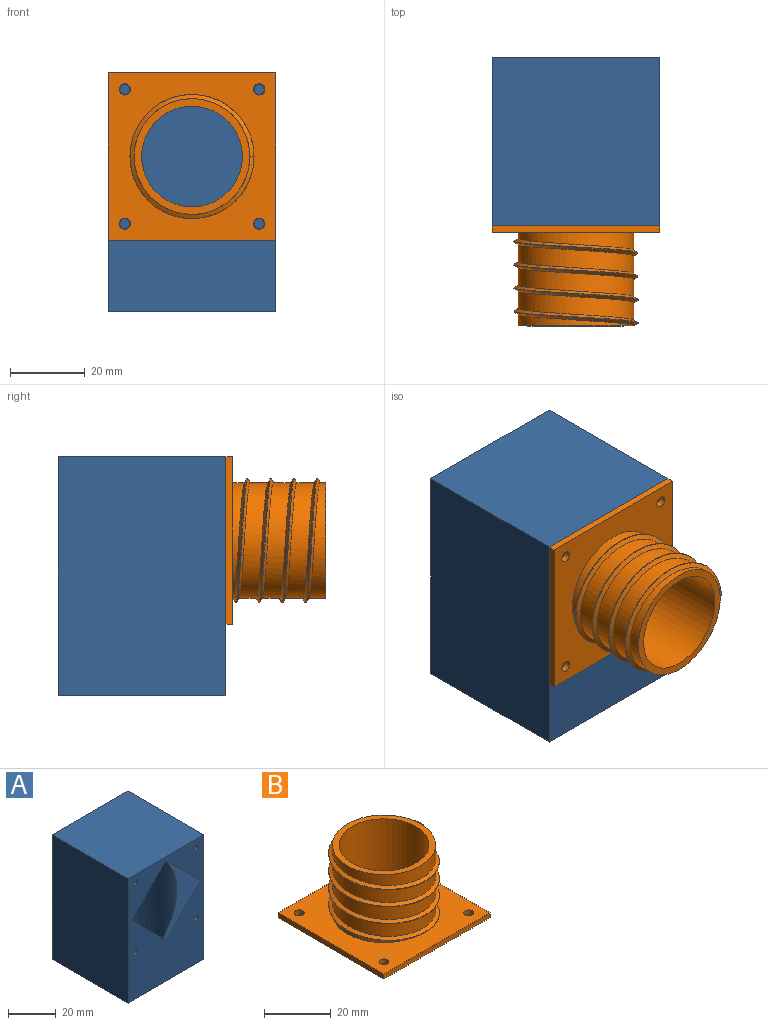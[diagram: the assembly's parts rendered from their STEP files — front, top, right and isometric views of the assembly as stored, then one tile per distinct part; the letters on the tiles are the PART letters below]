
ASSEMBLY  parts=2 mates=1
PART A: 22 faces, bbox 45x45x64 mm
  f0: plane 22.5x20.5mm, normal (0.71,0,0.71), area 185.5mm2, adj f5,f9,f11,f21
  f1: plane 20.5x20.5mm, normal (-0.71,0,0.71), area 127.5mm2, adj f8,f12,f21
  f2: plane 64x45mm, normal (1,0,0), area 2880mm2, adj f3,f5,f6,f7
  f3: plane 64x45mm, normal (0,1,0), area 2880mm2, adj f2,f4,f6,f7
  f4: plane 64x45mm, normal (-1,0,0), area 2880mm2, adj f3,f5,f6,f7
  f5: plane 64x45mm, normal (0,-1,0), area 2016.6mm2, adj f0,f2,f4,f6,f7,f8,f9,f11
  f6: plane 45x45mm, normal (0,0,1), area 2025mm2, adj f2,f3,f4,f5
  f7: plane 45x45mm, normal (0,0,-1), area 704.7mm2, adj f2,f3,f4,f5,f21
  f8: plane 43x20.5mm, normal (-0.71,0,-0.71), area 1246.6mm2, adj f1,f5,f9,f11,f12
  f9: plane 43x20.5mm, normal (0.71,0,-0.71), area 1246.6mm2, adj f0,f5,f8,f10,f12
  f10: plane 20.5x20.5mm, normal (0.71,0,0.71), area 127.5mm2, adj f9,f12,f21
  f11: plane 22.5x20.5mm, normal (-0.71,0,0.71), area 185.5mm2, adj f0,f5,f8,f21
  f12: plane 41x41mm, normal (0,-1,0), area 840.5mm2, adj f1,f8,f9,f10
  f13: cylinder r=1.35mm len=9mm, axis (0,-1,0), area 76.3mm2, adj f5,f14
  f14: plane 2.7x2.7mm, normal (0,-1,0), area 5.7mm2, adj f13
  f15: cylinder r=1.35mm len=9mm, axis (0,-1,0), area 76.3mm2, adj f5,f16
  f16: plane 2.7x2.7mm, normal (0,-1,0), area 5.7mm2, adj f15
  f17: cylinder r=1.35mm len=9mm, axis (0,-1,0), area 76.3mm2, adj f5,f18
  f18: plane 2.7x2.7mm, normal (0,-1,0), area 5.7mm2, adj f17
  f19: cylinder r=1.35mm len=9mm, axis (0,-1,0), area 76.3mm2, adj f5,f20
  f20: plane 2.7x2.7mm, normal (0,-1,0), area 5.7mm2, adj f19
  f21: cylinder r=20.5mm len=41.5mm, axis (0,0,-1), area 4385.9mm2, adj f0,f1,f7,f10,f11
PART B: 17 faces, bbox 45.3x45.3x27.1 mm
  f0: cylinder r=15.5mm len=31mm, axis (0,0,-1), area 1867.4mm2, adj f10,f12,f13,f14,f15
  f1: plane 45x1.8mm, normal (0,-1,0), area 81mm2, adj f2,f9,f10,f11
  f2: plane 45x1.8mm, normal (1,0,0), area 81mm2, adj f1,f3,f10,f11
  f3: plane 45x1.8mm, normal (0,1,0), area 81mm2, adj f2,f9,f10,f11
  f4: cylinder r=13.5mm len=27mm, axis (0,0,-1), area 2273.3mm2, adj f11,f12
  f5: cylinder r=1.5mm len=3mm, axis (0,0,-1), area 17mm2, adj f10,f11
  f6: cylinder r=1.5mm len=3mm, axis (0,0,-1), area 17mm2, adj f10,f11
  f7: cylinder r=1.5mm len=3mm, axis (0,0,-1), area 17mm2, adj f10,f11
  f8: cylinder r=1.5mm len=3mm, axis (0,0,-1), area 17mm2, adj f10,f11
  f9: plane 45x1.8mm, normal (-1,0,0), area 81mm2, adj f1,f3,f10,f11
  f10: plane 45.34x45.34mm, normal (0,0,1), area 1226.7mm2, adj f0,f1,f2,f3,f5,f6,f7,f8
  f11: plane 45x45mm, normal (0,0,-1), area 1424.2mm2, adj f1,f2,f3,f4,f5,f6,f7,f8
  f12: plane 31x31mm, normal (0,0,1), area 182.2mm2, adj f0,f4
  f13: plane 1.5x1.13mm, normal (0,-1,0), area 1mm2, adj f0,f14,f15,f16
  f14: bspline ~38.4x33.25mm, area 518.8mm2, adj f0,f10,f13,f16
  f15: bspline ~38.4x33.25mm, area 501mm2, adj f0,f10,f13,f16
  f16: cylinder r=16.63mm len=33.25mm, axis (0,0,1), area 84mm2, adj f10,f13,f14,f15
PLACE A t=(-59.5,5.25,-25.35)mm
PLACE B rot(axis=(1,0,0),90deg) t=(-59.5,-17.25,16.15)mm
MATE fastened A.f15 <-> B.f7  axis (0,-1,0) through (-77.5,-17.25,-1.85)mm
